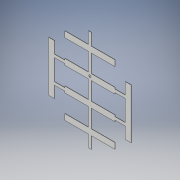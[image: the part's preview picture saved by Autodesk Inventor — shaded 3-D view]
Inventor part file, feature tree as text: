
AUTODESK INVENTOR PART (.ipt)
format: ipt  version: 2019 (Build 230136000, 136)  size: 175,616 bytes
history: native  units: mm
features: extrude x2, sketch x2
ambient origin geometry x8: Origin, YZ Plane, XZ Plane, XY Plane, X Axis, Y Axis, Z Axis, Center Point
bodies: Solid1 (feature_tree)
feature tree (4):
  extrude  "Extrusion1"  Depth=85.0mm
  extrude  "Extrusion2"  Depth=40.0mm
  sketch  "Sketch1"  dims[d0=172.0mm d12=85.0mm]
  sketch  "Sketch2"  dims[d13=10.0mm d14=40.0mm d16=40.5mm d17=10.0mm d19=10.0mm d21=20.25mm d22=20.25mm d23=30.5mm d24=10.0mm d25=85.0mm d26=20.961916mm d27=65.0mm d28=5.0mm d29=5.0mm d30=5.0mm d31=0.5mm d32=0.0mm d33=4.0mm d34=10.0mm d35=0.0mm]
